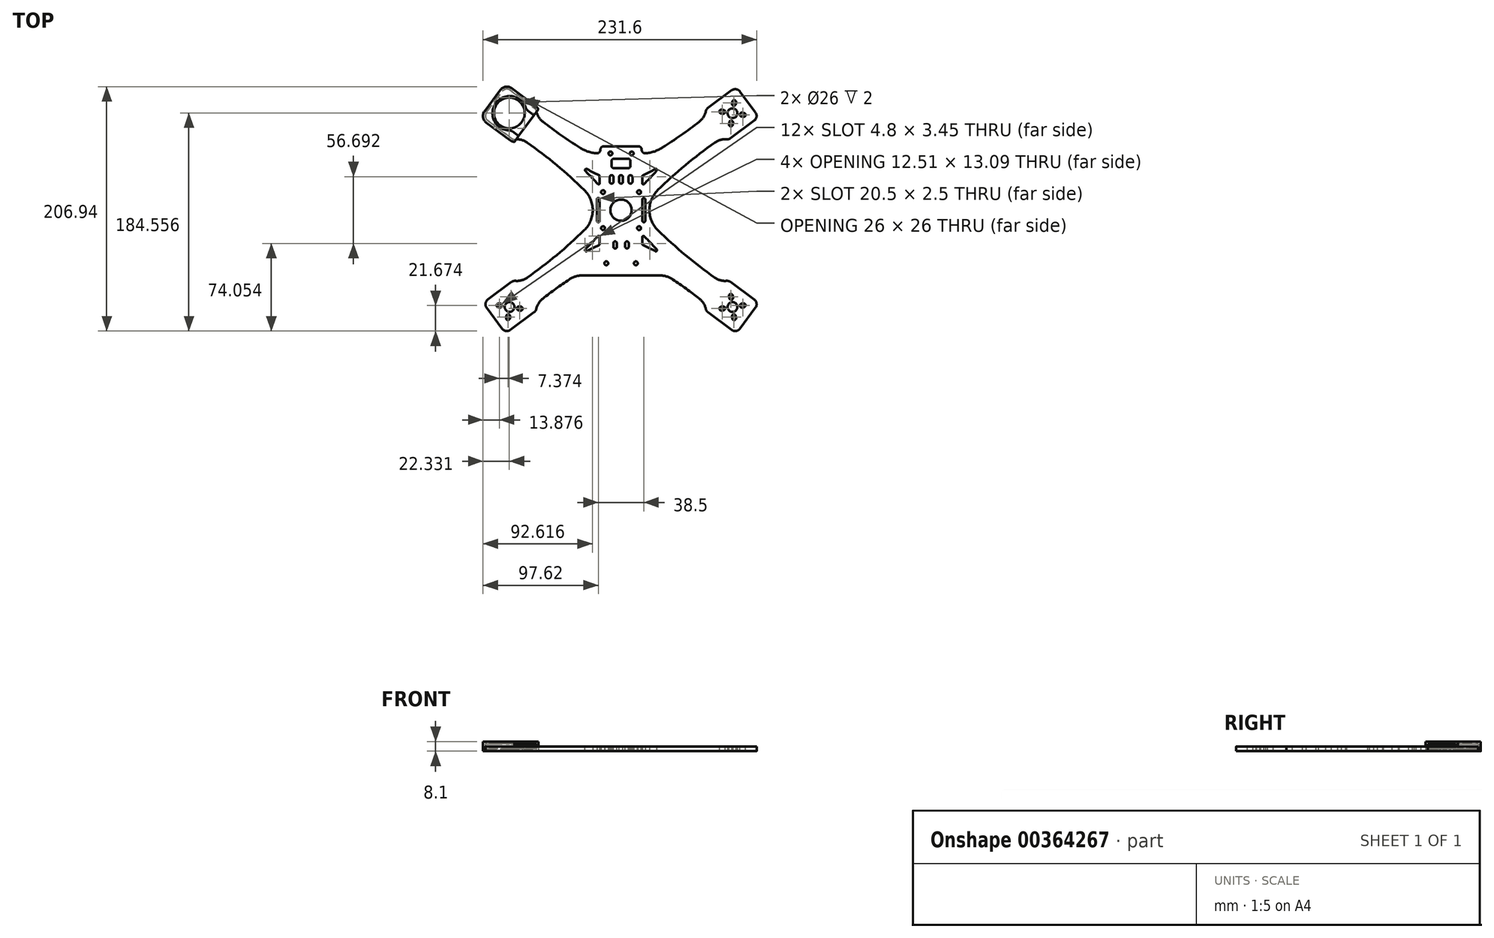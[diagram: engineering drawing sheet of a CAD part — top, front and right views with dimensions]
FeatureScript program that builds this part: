
annotation { "Feature Type Name" : "Feature", "Feature Type Description" : "" }
export const myFeature = defineFeature(function(context is Context, id is Id, definition is map)
    precondition{}
    {
        {
            var Q0;
            Q0=qCreatedBy(makeId("Top.planeOp"),FACE);
            var sketch = newSketch(context, id + "F0", { "sketchPlane" : qUnion([Q0])});
            skCircle(sketch, "E0", {"center": v(-15.25, 15.25) * mm, "radius": 1.63 * mm});
            skCircle(sketch, "E1", {"center": v(0, 0) * mm, "radius": 125 * mm, "construction": true});
            skCircle(sketch, "E2", {"center": v(-94.34, 82) * mm, "radius": 77.5 * mm, "construction": true});
            skLineSegment(sketch, "E3", {"start": v(0, 0) * mm, "end": v(-94.34, 82) * mm, "construction": true});
            skLineSegment(sketch, "E4", {"start": v(-94.34, 82) * mm, "end": v(0, 12) * mm, "construction": true});
            skLineSegment(sketch, "E5.bottom", {"start": v(-113.74, 82.7) * mm, "end": v(-100.63, 100.38) * mm});
            skLineSegment(sketch, "E5.left", {"start": v(-112.7, 75.71) * mm, "end": v(-92.67, 60.85) * mm});
            skLineSegment(sketch, "E5.right", {"start": v(-93.64, 101.41) * mm, "end": v(-73.6, 86.54) * mm});
            skLineSegment(sketch, "E6", {"start": v(-17.5, 54) * mm, "end": v(0, 54) * mm});
            skArc(sketch, "E7", {"start": v(-71.69, 83.57) * mm, "mid": v(-69.73, 78.72) * mm, "end": v(-66.21, 74.83) * mm});
            skArc(sketch, "E8", {"start": v(-79.32, 57.17) * mm, "mid": v(-84.06, 59.4) * mm, "end": v(-89.27, 59.88) * mm});
            skLineSegment(sketch, "E9", {"start": v(-19.25, 9) * mm, "end": v(-19.25, -9) * mm, "construction": true});
            skArc(sketch, "E10.0.startCap", {"start": v(-20.5, 9) * mm, "mid": v(-19.25, 10.25) * mm, "end": v(-18, 9) * mm});
            skArc(sketch, "E10.0.endCap", {"start": v(-18, -9) * mm, "mid": v(-19.25, -10.25) * mm, "end": v(-20.5, -9) * mm});
            skLineSegment(sketch, "E10.0.left", {"start": v(-18, 9) * mm, "end": v(-18, -9) * mm});
            skLineSegment(sketch, "E10.0.right", {"start": v(-20.5, 9) * mm, "end": v(-20.5, -9) * mm});
            skPoint(sketch, "E11.visualSharp", {"position": v(-116.72, 78.7) * mm});
            skArc(sketch, "E11.filletArc", {"start": v(-113.74, 82.7) * mm, "mid": v(-114.67, 79) * mm, "end": v(-112.7, 75.71) * mm});
            skPoint(sketch, "E12.visualSharp", {"position": v(-97.65, 104.4) * mm});
            skArc(sketch, "E12.filletArc", {"start": v(-93.64, 101.41) * mm, "mid": v(-97.35, 102.34) * mm, "end": v(-100.63, 100.38) * mm});
            skPoint(sketch, "E13.visualSharp", {"position": v(-91.02, 59.62) * mm});
            skArc(sketch, "E13.filletArc", {"start": v(-92.67, 60.85) * mm, "mid": v(-91.06, 60.05) * mm, "end": v(-89.27, 59.88) * mm});
            skPoint(sketch, "E14.visualSharp", {"position": v(-71.96, 85.32) * mm});
            skArc(sketch, "E14.filletArc", {"start": v(-71.69, 83.57) * mm, "mid": v(-72.37, 85.23) * mm, "end": v(-73.6, 86.54) * mm});
            skArc(sketch, "E15.MirrorCS", {"start": v(20.5, 9) * mm, "mid": v(19.25, 10.25) * mm, "end": v(18, 9) * mm});
            skArc(sketch, "E16.MirrorCS", {"start": v(71.69, 83.57) * mm, "mid": v(72.37, 85.23) * mm, "end": v(73.6, 86.54) * mm});
            skArc(sketch, "E17.MirrorCS", {"start": v(18, -9) * mm, "mid": v(19.25, -10.25) * mm, "end": v(20.5, -9) * mm});
            skArc(sketch, "E18.MirrorCS", {"start": v(92.67, 60.85) * mm, "mid": v(91.06, 60.05) * mm, "end": v(89.27, 59.88) * mm});
            skArc(sketch, "E19.MirrorCS", {"start": v(113.74, 82.7) * mm, "mid": v(114.67, 79) * mm, "end": v(112.7, 75.71) * mm});
            skArc(sketch, "E20.MirrorCS", {"start": v(71.69, 83.57) * mm, "mid": v(69.73, 78.72) * mm, "end": v(66.21, 74.83) * mm});
            skArc(sketch, "E21.MirrorCS", {"start": v(93.64, 101.41) * mm, "mid": v(97.35, 102.34) * mm, "end": v(100.63, 100.38) * mm});
            skArc(sketch, "E22.MirrorCS", {"start": v(79.32, 57.17) * mm, "mid": v(84.06, 59.4) * mm, "end": v(89.27, 59.88) * mm});
            skLineSegment(sketch, "E23.MirrorCS", {"start": v(20.5, 9) * mm, "end": v(20.5, -9) * mm});
            skLineSegment(sketch, "E24.MirrorCS", {"start": v(18, 9) * mm, "end": v(18, -9) * mm});
            skLineSegment(sketch, "E25.MirrorCS", {"start": v(19.25, 9) * mm, "end": v(19.25, -9) * mm, "construction": true});
            skLineSegment(sketch, "E26.MirrorCS", {"start": v(17.5, 54) * mm, "end": v(0, 54) * mm});
            skCircle(sketch, "E27.MirrorC", {"center": v(15.25, 15.25) * mm, "radius": 1.63 * mm});
            skPoint(sketch, "E28.MirrorP", {"position": v(71.96, 85.32) * mm});
            skLineSegment(sketch, "E29.MirrorCS", {"start": v(113.74, 82.7) * mm, "end": v(100.63, 100.38) * mm});
            skLineSegment(sketch, "E30.MirrorCS", {"start": v(0, 0) * mm, "end": v(94.34, 82) * mm, "construction": true});
            skLineSegment(sketch, "E31.MirrorCS", {"start": v(94.34, 82) * mm, "end": v(0, 12) * mm, "construction": true});
            skCircle(sketch, "E32.MirrorC", {"center": v(94.34, 82) * mm, "radius": 77.5 * mm, "construction": true});
            skLineSegment(sketch, "E33.MirrorCS", {"start": v(112.7, 75.71) * mm, "end": v(92.67, 60.85) * mm});
            skLineSegment(sketch, "E34.MirrorCS", {"start": v(93.64, 101.41) * mm, "end": v(73.6, 86.54) * mm});
            skPoint(sketch, "E35.MirrorP", {"position": v(97.65, 104.4) * mm});
            skPoint(sketch, "E36.MirrorP", {"position": v(91.02, 59.62) * mm});
            skPoint(sketch, "E37.MirrorP", {"position": v(116.72, 78.7) * mm});
            skArc(sketch, "E38.MirrorCS", {"start": v(-71.69, -83.57) * mm, "mid": v(-72.37, -85.23) * mm, "end": v(-73.6, -86.54) * mm});
            skArc(sketch, "E39.MirrorCS", {"start": v(-92.67, -60.85) * mm, "mid": v(-91.06, -60.05) * mm, "end": v(-89.27, -59.88) * mm});
            skArc(sketch, "E40.MirrorCS", {"start": v(71.69, -83.57) * mm, "mid": v(72.37, -85.23) * mm, "end": v(73.6, -86.54) * mm});
            skArc(sketch, "E41.MirrorCS", {"start": v(92.67, -60.85) * mm, "mid": v(91.06, -60.05) * mm, "end": v(89.27, -59.88) * mm});
            skArc(sketch, "E42.MirrorCS", {"start": v(79.32, -57.17) * mm, "mid": v(84.06, -59.4) * mm, "end": v(89.27, -59.88) * mm});
            skArc(sketch, "E43.MirrorCS", {"start": v(93.64, -101.41) * mm, "mid": v(97.35, -102.34) * mm, "end": v(100.63, -100.38) * mm});
            skArc(sketch, "E44.MirrorCS", {"start": v(-93.64, -101.41) * mm, "mid": v(-97.35, -102.34) * mm, "end": v(-100.63, -100.38) * mm});
            skArc(sketch, "E45.MirrorCS", {"start": v(-79.32, -57.17) * mm, "mid": v(-84.06, -59.4) * mm, "end": v(-89.27, -59.88) * mm});
            skArc(sketch, "E46.MirrorCS", {"start": v(-71.69, -83.57) * mm, "mid": v(-69.73, -78.72) * mm, "end": v(-66.21, -74.83) * mm});
            skArc(sketch, "E47.MirrorCS", {"start": v(113.74, -82.7) * mm, "mid": v(114.67, -79) * mm, "end": v(112.7, -75.71) * mm});
            skArc(sketch, "E48.MirrorCS", {"start": v(71.69, -83.57) * mm, "mid": v(69.73, -78.72) * mm, "end": v(66.21, -74.83) * mm});
            skArc(sketch, "E49.MirrorCS", {"start": v(-113.74, -82.7) * mm, "mid": v(-114.67, -79) * mm, "end": v(-112.7, -75.71) * mm});
            skCircle(sketch, "E50.MirrorC", {"center": v(-15.25, -15.25) * mm, "radius": 1.63 * mm});
            skCircle(sketch, "E51.MirrorC", {"center": v(15.25, -15.25) * mm, "radius": 1.63 * mm});
            skPoint(sketch, "E52.MirrorP", {"position": v(-71.96, -85.32) * mm});
            skLineSegment(sketch, "E53.MirrorCS", {"start": v(93.64, -101.41) * mm, "end": v(73.6, -86.54) * mm});
            skPoint(sketch, "E54.MirrorP", {"position": v(116.72, -78.7) * mm});
            skLineSegment(sketch, "E55.MirrorCS", {"start": v(112.7, -75.71) * mm, "end": v(92.67, -60.85) * mm});
            skPoint(sketch, "E56.MirrorP", {"position": v(91.02, -59.62) * mm});
            skPoint(sketch, "E57.MirrorP", {"position": v(-91.02, -59.62) * mm});
            skLineSegment(sketch, "E58.MirrorCS", {"start": v(-93.64, -101.41) * mm, "end": v(-73.6, -86.54) * mm});
            skLineSegment(sketch, "E59.MirrorCS", {"start": v(-112.7, -75.71) * mm, "end": v(-92.67, -60.85) * mm});
            skLineSegment(sketch, "E60.MirrorCS", {"start": v(-113.74, -82.7) * mm, "end": v(-100.63, -100.38) * mm});
            skPoint(sketch, "E61.MirrorP", {"position": v(-97.65, -104.4) * mm});
            skLineSegment(sketch, "E62.MirrorCS", {"start": v(113.74, -82.7) * mm, "end": v(100.63, -100.38) * mm});
            skPoint(sketch, "E63.MirrorP", {"position": v(97.65, -104.4) * mm});
            skPoint(sketch, "E64.MirrorP", {"position": v(-116.72, -78.7) * mm});
            skPoint(sketch, "E65.MirrorP", {"position": v(71.96, -85.32) * mm});
            skCircle(sketch, "E66.MirrorC", {"center": v(-94.34, -82) * mm, "radius": 77.5 * mm, "construction": true});
            skCircle(sketch, "E67.MirrorC", {"center": v(94.34, -82) * mm, "radius": 77.5 * mm, "construction": true});
            skCircle(sketch, "E68", {"center": v(-94.34, 82) * mm, "radius": 4.12 * mm});
            skCircle(sketch, "E69.MirrorC", {"center": v(94.34, 82) * mm, "radius": 4.12 * mm});
            skCircle(sketch, "E70.MirrorC", {"center": v(-94.34, -82) * mm, "radius": 4.12 * mm});
            skCircle(sketch, "E71.MirrorC", {"center": v(94.34, -82) * mm, "radius": 4.12 * mm});
            skArc(sketch, "E72", {"start": v(-31.15, 16.99) * mm, "mid": v(-54.45, 38.02) * mm, "end": v(-79.32, 57.17) * mm});
            skArc(sketch, "E73.MirrorCS", {"start": v(31.15, 16.99) * mm, "mid": v(54.45, 38.02) * mm, "end": v(79.32, 57.17) * mm});
            skArc(sketch, "E74.MirrorCS", {"start": v(-31.15, -16.99) * mm, "mid": v(-54.45, -38.02) * mm, "end": v(-79.32, -57.17) * mm});
            skArc(sketch, "E75.MirrorCS", {"start": v(31.15, -16.99) * mm, "mid": v(54.45, -38.02) * mm, "end": v(79.32, -57.17) * mm});
            skArc(sketch, "E76.trimOffspring", {"start": v(-34.92, 52.85) * mm, "mid": v(-50.83, 63.47) * mm, "end": v(-66.21, 74.83) * mm});
            skArc(sketch, "E77.MirrorCS", {"start": v(34.92, 52.85) * mm, "mid": v(50.83, 63.47) * mm, "end": v(66.21, 74.83) * mm});
            skArc(sketch, "E78.MirrorCS", {"start": v(43.8, -58.64) * mm, "mid": v(55.14, -66.54) * mm, "end": v(66.21, -74.83) * mm});
            skArc(sketch, "E79.MirrorCS", {"start": v(-43.8, -58.64) * mm, "mid": v(-55.14, -66.54) * mm, "end": v(-66.21, -74.83) * mm});
            skLineSegment(sketch, "E80", {"start": v(-32.65, -55.25) * mm, "end": v(32.65, -55.25) * mm});
            skPoint(sketch, "E81.visualSharp", {"position": v(-38.65, -55.25) * mm});
            skArc(sketch, "E81.filletArc", {"start": v(-32.65, -55.25) * mm, "mid": v(-38.48, -56.12) * mm, "end": v(-43.8, -58.64) * mm});
            skPoint(sketch, "E82.visualSharp", {"position": v(38.65, -55.25) * mm});
            skArc(sketch, "E82.filletArc", {"start": v(43.8, -58.64) * mm, "mid": v(38.48, -56.12) * mm, "end": v(32.65, -55.25) * mm});
            skArc(sketch, "E83.filletArc", {"start": v(-34.92, 52.85) * mm, "mid": v(-28.12, 49.62) * mm, "end": v(-20.75, 48.1) * mm});
            skArc(sketch, "E84.filletArc", {"start": v(20.75, 48.1) * mm, "mid": v(28.12, 49.62) * mm, "end": v(34.92, 52.85) * mm});
            skCircle(sketch, "E85", {"center": v(-9, 48) * mm, "radius": 1.63 * mm});
            skLineSegment(sketch, "E86", {"start": v(-17.5, 54) * mm, "end": v(-17.5, 51.1) * mm});
            skLineSegment(sketch, "E87", {"start": v(17.5, 54) * mm, "end": v(17.5, 51.1) * mm});
            skPoint(sketch, "E88.visualSharp", {"position": v(-17.5, 48) * mm});
            skArc(sketch, "E88.filletArc", {"start": v(-20.75, 48.1) * mm, "mid": v(-18.47, 48.88) * mm, "end": v(-17.5, 51.1) * mm});
            skPoint(sketch, "E89.visualSharp", {"position": v(17.5, 48) * mm});
            skArc(sketch, "E89.filletArc", {"start": v(17.5, 51.1) * mm, "mid": v(18.47, 48.88) * mm, "end": v(20.75, 48.1) * mm});
            skCircle(sketch, "E90.MirrorC", {"center": v(9, 48) * mm, "radius": 1.63 * mm});
            skPoint(sketch, "E91.visualSharp", {"position": v(-14.76, 0) * mm});
            skArc(sketch, "E91.filletArc", {"start": v(-31.15, -16.99) * mm, "mid": v(-24, 0) * mm, "end": v(-31.15, 16.99) * mm});
            skPoint(sketch, "E92.visualSharp", {"position": v(14.76, 0) * mm});
            skArc(sketch, "E92.filletArc", {"start": v(31.15, 16.99) * mm, "mid": v(24, 0) * mm, "end": v(31.15, -16.99) * mm});
            skCircle(sketch, "E93", {"center": v(-12.5, -45) * mm, "radius": 1.63 * mm});
            skCircle(sketch, "E94.MirrorC", {"center": v(12.5, -45) * mm, "radius": 1.63 * mm});
            skSolve(sketch);
        }
        {
            var Q0;
            Q0=qSketchRegion(id+"F0",true);
            extrude(context, id + "F1", {"entities" : qUnion([Q0]), "depth" : 4 * mm});
        }
        {
            var Q0;
            Q0=makeQuery(id+"F1.opExtrude","CAP_FACE",FACE,{"disambiguationData":[OSD([sQuery(id+"F0.wireOp",EDGE,"E0"),sQuery(id+"F0.wireOp",EDGE,"bZv11kwC-7Zwh-qoiM-MuVD-QWfY3VRXTvEb"),sQuery(id+"F0.wireOp",EDGE,"Hg7IfRWj-3ALA-Ly6Y-QmXC-kUpIx1ZQ4bFj"),sQuery(id+"F0.wireOp",EDGE,"i2Ly1i0H-hUQD-DSDW-V0AA-PaiG6Uw8rzNW"),sQuery(id+"F0.wireOp",EDGE,"E5.bottom"),sQuery(id+"F0.wireOp",EDGE,"E5.left"),sQuery(id+"F0.wireOp",EDGE,"E5.right"),sQuery(id+"F0.wireOp",EDGE,"E7"),sQuery(id+"F0.wireOp",EDGE,"E8"),sQuery(id+"F0.wireOp",EDGE,"26a3e7e2-4a16-4030-acf8-3f1fbd5a5a34.filletArc"),sQuery(id+"F0.wireOp",EDGE,"E10.0.startCap"),sQuery(id+"F0.wireOp",EDGE,"E10.0.endCap"),sQuery(id+"F0.wireOp",EDGE,"E10.0.left"),sQuery(id+"F0.wireOp",EDGE,"E10.0.right"),sQuery(id+"F0.wireOp",EDGE,"E11.filletArc"),sQuery(id+"F0.wireOp",EDGE,"E12.filletArc"),sQuery(id+"F0.wireOp",EDGE,"E13.filletArc"),sQuery(id+"F0.wireOp",EDGE,"E14.filletArc"),sQuery(id+"F0.wireOp",EDGE,"E15.MirrorCS"),sQuery(id+"F0.wireOp",EDGE,"E16.MirrorCS"),sQuery(id+"F0.wireOp",EDGE,"E17.MirrorCS"),sQuery(id+"F0.wireOp",EDGE,"E18.MirrorCS"),sQuery(id+"F0.wireOp",EDGE,"E19.MirrorCS"),sQuery(id+"F0.wireOp",EDGE,"E20.MirrorCS"),sQuery(id+"F0.wireOp",EDGE,"b7ecff87-ac14-4935-8a3e-caa413c79c2e13.MirrorCS"),sQuery(id+"F0.wireOp",EDGE,"E21.MirrorCS"),sQuery(id+"F0.wireOp",EDGE,"E22.MirrorCS"),sQuery(id+"F0.wireOp",EDGE,"E23.MirrorCS"),sQuery(id+"F0.wireOp",EDGE,"E24.MirrorCS"),sQuery(id+"F0.wireOp",EDGE,"b7ecff87-ac14-4935-8a3e-caa413c79c2e23.MirrorCS"),sQuery(id+"F0.wireOp",EDGE,"E27.MirrorC"),sQuery(id+"F0.wireOp",EDGE,"E29.MirrorCS"),sQuery(id+"F0.wireOp",EDGE,"b7ecff87-ac14-4935-8a3e-caa413c79c2e29.MirrorCS"),sQuery(id+"F0.wireOp",EDGE,"E33.MirrorCS"),sQuery(id+"F0.wireOp",EDGE,"E34.MirrorCS"),sQuery(id+"F0.wireOp",EDGE,"b7ecff87-ac14-4935-8a3e-caa413c79c2e39.MirrorCS"),sQuery(id+"F0.wireOp",EDGE,"E38.MirrorCS"),sQuery(id+"F0.wireOp",EDGE,"E39.MirrorCS"),sQuery(id+"F0.wireOp",EDGE,"E40.MirrorCS"),sQuery(id+"F0.wireOp",EDGE,"E41.MirrorCS"),sQuery(id+"F0.wireOp",EDGE,"E42.MirrorCS"),sQuery(id+"F0.wireOp",EDGE,"E43.MirrorCS"),sQuery(id+"F0.wireOp",EDGE,"E44.MirrorCS"),sQuery(id+"F0.wireOp",EDGE,"E45.MirrorCS"),sQuery(id+"F0.wireOp",EDGE,"E46.MirrorCS"),sQuery(id+"F0.wireOp",EDGE,"E47.MirrorCS"),sQuery(id+"F0.wireOp",EDGE,"E48.MirrorCS"),sQuery(id+"F0.wireOp",EDGE,"E49.MirrorCS"),sQuery(id+"F0.wireOp",EDGE,"E50.MirrorC"),sQuery(id+"F0.wireOp",EDGE,"E51.MirrorC"),sQuery(id+"F0.wireOp",EDGE,"7b8357ce-6b81-4621-bb5f-09712327f37e37.MirrorCS"),sQuery(id+"F0.wireOp",EDGE,"E53.MirrorCS"),sQuery(id+"F0.wireOp",EDGE,"E55.MirrorCS"),sQuery(id+"F0.wireOp",EDGE,"E58.MirrorCS"),sQuery(id+"F0.wireOp",EDGE,"E59.MirrorCS"),sQuery(id+"F0.wireOp",EDGE,"E60.MirrorCS"),sQuery(id+"F0.wireOp",EDGE,"7b8357ce-6b81-4621-bb5f-09712327f37e49.MirrorCS"),sQuery(id+"F0.wireOp",EDGE,"7b8357ce-6b81-4621-bb5f-09712327f37e50.MirrorCS"),sQuery(id+"F0.wireOp",EDGE,"E62.MirrorCS"),sQuery(id+"F0.wireOp",EDGE,"7b8357ce-6b81-4621-bb5f-09712327f37e55.MirrorCS"),sQuery(id+"F0.wireOp",EDGE,"d83ce2ea-2607-4b6c-a04d-38c7ae4304c90.MirrorCS"),sQuery(id+"F0.wireOp",EDGE,"b69c18a7-e43b-42be-b145-92b5204aa2ed0.MirrorCS"),sQuery(id+"F0.wireOp",EDGE,"a0707623-7043-4475-b436-6124989390590.MirrorCS"),sQuery(id+"F0.wireOp",EDGE,"4f61c261-c1ce-4229-8802-2f54477ed9b20.MirrorCS"),sQuery(id+"F0.wireOp",EDGE,"PiAP6XZh-xq8d-wj9O-Epc7-kF4WUdjTUHBz"),sQuery(id+"F0.wireOp",EDGE,"26e37ba6-caeb-4f33-ab48-1d1fe7035cbd0.MirrorC"),sQuery(id+"F0.wireOp",EDGE,"2yan8IeJ-tOHB-Kgj5-MnLH-DyiSyil4pG3S"),sQuery(id+"F0.wireOp",EDGE,"gHJ05LQx-usyR-kV3a-hPzh-QXjW5T1wXW1p"),sQuery(id+"F0.wireOp",EDGE,"uchXSoDE-KjdM-uTwm-rJXX-9rzWfyOP3x4Z"),sQuery(id+"F0.wireOp",EDGE,"8eu2Gxre-rbZ0-mDo1-W97T-pc3IviFYihye"),sQuery(id+"F0.wireOp",EDGE,"eavqlNsN-eOFr-pDPr-DEgw-YRCTYlhg5u3t"),sQuery(id+"F0.wireOp",EDGE,"Bw8slYh4-NEub-OYFD-4ET6-0dd0G63bUOwi"),sQuery(id+"F0.wireOp",EDGE,"af94888a-cba0-45cd-aecc-a0270221dd82.trimOffspring"),sQuery(id+"F0.wireOp",EDGE,"36199e4a-d6a7-49c4-a502-27b3488fd5e6.filletArc"),sQuery(id+"F0.wireOp",EDGE,"9e30e6b1-65ef-4937-9bd8-18fed2c5f1090.MirrorCS"),sQuery(id+"F0.wireOp",EDGE,"31f30485-6f3e-4795-917b-55e225d339680.MirrorCS"),sQuery(id+"F0.wireOp",EDGE,"86aa6092-d3c3-42aa-99ce-90435510c5960.MirrorCS"),sQuery(id+"F0.wireOp",EDGE,"5a69975c-1d9b-4b23-809c-878e26df679d0.MirrorCS"),sQuery(id+"F0.wireOp",EDGE,"8025df49-7d22-4dba-957a-6396c4b11ce90.MirrorCS"),sQuery(id+"F0.wireOp",EDGE,"b23088bf-ab4c-4e44-9a43-da8ffa8499a00.MirrorCS"),sQuery(id+"F0.wireOp",EDGE,"d9780cfa-9ead-4347-a629-1b1a594d6e410.MirrorCS"),sQuery(id+"F0.wireOp",EDGE,"68fec51b-96b4-4918-b858-b07c475e679e0.MirrorCS"),sQuery(id+"F0.wireOp",EDGE,"b72a6ee6-5ab0-4ed6-be8f-ffada714514d0.MirrorCS"),sQuery(id+"F0.wireOp",EDGE,"8773bbf2-5ef2-485a-bde0-34addb67332b0.MirrorCS"),sQuery(id+"F0.wireOp",EDGE,"ce348970-fad1-4eb4-9c27-5204bf570fdb0.MirrorCS"),sQuery(id+"F0.wireOp",EDGE,"404c4f6d-7f85-4f91-8924-7a461248f6590.MirrorCS"),sQuery(id+"F0.wireOp",EDGE,"TJ6xSgkY-RBVc-ApbF-Rnxn-nYxT4uNRJTxX"),sQuery(id+"F0.wireOp",EDGE,"hn5H7zRm-rU73-VfAX-dvYv-k9Lax7dM8k8G"),sQuery(id+"F0.wireOp",EDGE,"UOzbpYJr-Rpqu-ZeE8-tXKC-t89DSqlBGB8Q"),sQuery(id+"F0.wireOp",EDGE,"YxJJHRqV-amlc-LN3y-haml-tisoirnnfRJY"),sQuery(id+"F0.wireOp",EDGE,"033e0fe7-d3c1-42f5-ae8f-adbb043379e8.filletArc"),sQuery(id+"F0.wireOp",EDGE,"afa99035-e99d-4a73-974f-5500cdf2138a.filletArc"),sQuery(id+"F0.wireOp",EDGE,"9i3ea3iE-3Dll-Ek6R-PhGe-V1XcnAEkodY1.bottom"),sQuery(id+"F0.wireOp",EDGE,"9i3ea3iE-3Dll-Ek6R-PhGe-V1XcnAEkodY1.left"),sQuery(id+"F0.wireOp",EDGE,"9i3ea3iE-3Dll-Ek6R-PhGe-V1XcnAEkodY1.right"),sQuery(id+"F0.wireOp",EDGE,"1382622d-cae2-4c61-9f5c-b8746732d9fe0.MirrorCS"),sQuery(id+"F0.wireOp",EDGE,"0d70f9a0-c1ad-434e-a495-165a5a764f960.MirrorCS"),sQuery(id+"F0.wireOp",EDGE,"1f8d5036-162d-4fc3-b441-7a8ab5cd179e0.MirrorCS"),sQuery(id+"F0.wireOp",EDGE,"Km0E7gO1-P8tX-SnyZ-vo1L-W35BEzFtr7vK"),sQuery(id+"F0.wireOp",EDGE,"4twT0r3F-PA9R-wz1e-iyg0-9RBk79VGwi7g"),sQuery(id+"F0.wireOp",EDGE,"14bccf5c-bb99-48c5-a73f-577480a40b4e0.MirrorCS"),sQuery(id+"F0.wireOp",EDGE,"a123c59d-a695-4b06-9137-5aaff9e2b4be0.MirrorCS"),sQuery(id+"F0.wireOp",EDGE,"E68"),sQuery(id+"F0.wireOp",EDGE,"E69.MirrorC"),sQuery(id+"F0.wireOp",EDGE,"E70.MirrorC"),sQuery(id+"F0.wireOp",EDGE,"E71.MirrorC")])],"isStart":false});
            var sketch = newSketch(context, id + "F2", { "sketchPlane" : qUnion([Q0])});
            skCircle(sketch, "E95", {"center": v(-94.34, 82) * mm, "radius": 7.95 * mm, "construction": true});
            skCircle(sketch, "E96", {"center": v(-94.34, 82) * mm, "radius": 9.55 * mm, "construction": true});
            skLineSegment(sketch, "E97", {"start": v(-95.5, 89.87) * mm, "end": v(-95.74, 91.45) * mm, "construction": true});
            skLineSegment(sketch, "E98", {"start": v(-95.5, 89.87) * mm, "end": v(-94.34, 82) * mm, "construction": true});
            skLineSegment(sketch, "E99", {"start": v(-94.34, 82) * mm, "end": v(0, 12) * mm, "construction": true});
            skArc(sketch, "E100.0.startCap", {"start": v(-93.9, 90.1) * mm, "mid": v(-95.27, 88.26) * mm, "end": v(-97.11, 89.63) * mm});
            skArc(sketch, "E100.0.endCap", {"start": v(-97.34, 91.22) * mm, "mid": v(-95.98, 93.06) * mm, "end": v(-94.13, 91.7) * mm});
            skLineSegment(sketch, "E100.0.left", {"start": v(-97.11, 89.63) * mm, "end": v(-97.34, 91.22) * mm});
            skLineSegment(sketch, "E100.0.right", {"start": v(-93.9, 90.1) * mm, "end": v(-94.13, 91.7) * mm});
            skLineSegment(sketch, "E101.1.0", {"start": v(-102.2, 80.84) * mm, "end": v(-103.79, 80.6) * mm, "construction": true});
            skArc(sketch, "E101.1.1", {"start": v(-102.44, 82.45) * mm, "mid": v(-100.6, 81.08) * mm, "end": v(-101.96, 79.24) * mm});
            skLineSegment(sketch, "E101.1.2", {"start": v(-101.96, 79.24) * mm, "end": v(-103.55, 79) * mm});
            skLineSegment(sketch, "E101.1.3", {"start": v(-102.44, 82.45) * mm, "end": v(-104.02, 82.22) * mm});
            skArc(sketch, "E101.1.4", {"start": v(-103.55, 79) * mm, "mid": v(-105.4, 80.37) * mm, "end": v(-104.02, 82.22) * mm});
            skLineSegment(sketch, "E101.2.0", {"start": v(-93.17, 74.14) * mm, "end": v(-92.94, 72.56) * mm, "construction": true});
            skArc(sketch, "E101.2.1", {"start": v(-94.78, 73.9) * mm, "mid": v(-93.41, 75.75) * mm, "end": v(-91.57, 74.38) * mm});
            skLineSegment(sketch, "E101.2.2", {"start": v(-91.57, 74.38) * mm, "end": v(-91.33, 72.8) * mm});
            skLineSegment(sketch, "E101.2.3", {"start": v(-94.78, 73.9) * mm, "end": v(-94.55, 72.32) * mm});
            skArc(sketch, "E101.2.4", {"start": v(-91.33, 72.8) * mm, "mid": v(-92.7, 70.95) * mm, "end": v(-94.55, 72.32) * mm});
            skLineSegment(sketch, "E101.3.0", {"start": v(-86.47, 83.17) * mm, "end": v(-84.9, 83.4) * mm, "construction": true});
            skArc(sketch, "E101.3.1", {"start": v(-86.24, 81.56) * mm, "mid": v(-88.08, 82.93) * mm, "end": v(-86.71, 84.78) * mm});
            skLineSegment(sketch, "E101.3.2", {"start": v(-86.71, 84.78) * mm, "end": v(-85.13, 85.01) * mm});
            skLineSegment(sketch, "E101.3.3", {"start": v(-86.24, 81.56) * mm, "end": v(-84.65, 81.8) * mm});
            skArc(sketch, "E101.3.4", {"start": v(-85.13, 85.01) * mm, "mid": v(-83.28, 83.64) * mm, "end": v(-84.65, 81.8) * mm});
            skLineSegment(sketch, "E102.MirrorCS", {"start": v(95.5, 89.87) * mm, "end": v(95.74, 91.45) * mm, "construction": true});
            skLineSegment(sketch, "E103.MirrorCS", {"start": v(93.9, 90.1) * mm, "end": v(94.13, 91.7) * mm});
            skLineSegment(sketch, "E104.MirrorCS", {"start": v(102.2, 80.84) * mm, "end": v(103.79, 80.6) * mm, "construction": true});
            skLineSegment(sketch, "E105.MirrorCS", {"start": v(102.44, 82.45) * mm, "end": v(104.02, 82.22) * mm});
            skLineSegment(sketch, "E106.MirrorCS", {"start": v(86.71, 84.78) * mm, "end": v(85.13, 85.01) * mm});
            skLineSegment(sketch, "E107.MirrorCS", {"start": v(97.11, 89.63) * mm, "end": v(97.34, 91.22) * mm});
            skLineSegment(sketch, "E108.MirrorCS", {"start": v(94.78, 73.9) * mm, "end": v(94.55, 72.32) * mm});
            skLineSegment(sketch, "E109.MirrorCS", {"start": v(86.24, 81.56) * mm, "end": v(84.65, 81.8) * mm});
            skArc(sketch, "E110.MirrorCS", {"start": v(102.44, 82.45) * mm, "mid": v(100.6, 81.08) * mm, "end": v(101.96, 79.24) * mm});
            skArc(sketch, "E111.MirrorCS", {"start": v(97.34, 91.22) * mm, "mid": v(95.98, 93.06) * mm, "end": v(94.13, 91.7) * mm});
            skArc(sketch, "E112.MirrorCS", {"start": v(91.33, 72.8) * mm, "mid": v(92.7, 70.95) * mm, "end": v(94.55, 72.32) * mm});
            skLineSegment(sketch, "E113.MirrorCS", {"start": v(93.17, 74.14) * mm, "end": v(92.94, 72.56) * mm, "construction": true});
            skArc(sketch, "E114.MirrorCS", {"start": v(85.13, 85.01) * mm, "mid": v(83.28, 83.64) * mm, "end": v(84.65, 81.8) * mm});
            skArc(sketch, "E115.MirrorCS", {"start": v(103.55, 79) * mm, "mid": v(105.4, 80.37) * mm, "end": v(104.02, 82.22) * mm});
            skLineSegment(sketch, "E116.MirrorCS", {"start": v(86.47, 83.17) * mm, "end": v(84.9, 83.4) * mm, "construction": true});
            skLineSegment(sketch, "E117.MirrorCS", {"start": v(101.96, 79.24) * mm, "end": v(103.55, 79) * mm});
            skArc(sketch, "E118.MirrorCS", {"start": v(94.78, 73.9) * mm, "mid": v(93.41, 75.75) * mm, "end": v(91.57, 74.38) * mm});
            skArc(sketch, "E119.MirrorCS", {"start": v(86.24, 81.56) * mm, "mid": v(88.08, 82.93) * mm, "end": v(86.71, 84.78) * mm});
            skLineSegment(sketch, "E120.MirrorCS", {"start": v(91.57, 74.38) * mm, "end": v(91.33, 72.8) * mm});
            skArc(sketch, "E121.MirrorCS", {"start": v(93.9, 90.1) * mm, "mid": v(95.27, 88.26) * mm, "end": v(97.11, 89.63) * mm});
            skPoint(sketch, "E122.MirrorP", {"position": v(94.34, 82) * mm});
            skCircle(sketch, "E123.MirrorC", {"center": v(94.34, 82) * mm, "radius": 9.55 * mm, "construction": true});
            skCircle(sketch, "E124.MirrorC", {"center": v(94.34, 82) * mm, "radius": 7.95 * mm, "construction": true});
            skLineSegment(sketch, "E125.MirrorCS", {"start": v(95.5, 89.87) * mm, "end": v(94.34, 82) * mm, "construction": true});
            skLineSegment(sketch, "E126.MirrorCS", {"start": v(-95.5, -89.87) * mm, "end": v(-95.74, -91.45) * mm, "construction": true});
            skLineSegment(sketch, "E127.MirrorCS", {"start": v(-93.9, -90.1) * mm, "end": v(-94.13, -91.7) * mm});
            skArc(sketch, "E128.MirrorCS", {"start": v(-93.9, -90.1) * mm, "mid": v(-95.27, -88.26) * mm, "end": v(-97.11, -89.63) * mm});
            skLineSegment(sketch, "E129.MirrorCS", {"start": v(-95.5, -89.87) * mm, "end": v(-94.34, -82) * mm, "construction": true});
            skLineSegment(sketch, "E130.MirrorCS", {"start": v(-97.11, -89.63) * mm, "end": v(-97.34, -91.22) * mm});
            skLineSegment(sketch, "E131.MirrorCS", {"start": v(-102.44, -82.45) * mm, "end": v(-104.02, -82.22) * mm});
            skLineSegment(sketch, "E132.MirrorCS", {"start": v(86.24, -81.56) * mm, "end": v(84.65, -81.8) * mm});
            skArc(sketch, "E133.MirrorCS", {"start": v(86.24, -81.56) * mm, "mid": v(88.08, -82.93) * mm, "end": v(86.71, -84.78) * mm});
            skLineSegment(sketch, "E134.MirrorCS", {"start": v(97.11, -89.63) * mm, "end": v(97.34, -91.22) * mm});
            skArc(sketch, "E135.MirrorCS", {"start": v(-102.44, -82.45) * mm, "mid": v(-100.6, -81.08) * mm, "end": v(-101.96, -79.24) * mm});
            skLineSegment(sketch, "E136.MirrorCS", {"start": v(-101.96, -79.24) * mm, "end": v(-103.55, -79) * mm});
            skLineSegment(sketch, "E137.MirrorCS", {"start": v(-102.2, -80.84) * mm, "end": v(-103.79, -80.6) * mm, "construction": true});
            skArc(sketch, "E138.MirrorCS", {"start": v(-103.55, -79) * mm, "mid": v(-105.4, -80.37) * mm, "end": v(-104.02, -82.22) * mm});
            skLineSegment(sketch, "E139.MirrorCS", {"start": v(102.2, -80.84) * mm, "end": v(103.79, -80.6) * mm, "construction": true});
            skLineSegment(sketch, "E140.MirrorCS", {"start": v(86.47, -83.17) * mm, "end": v(84.9, -83.4) * mm, "construction": true});
            skLineSegment(sketch, "E141.MirrorCS", {"start": v(101.96, -79.24) * mm, "end": v(103.55, -79) * mm});
            skArc(sketch, "E142.MirrorCS", {"start": v(102.44, -82.45) * mm, "mid": v(100.6, -81.08) * mm, "end": v(101.96, -79.24) * mm});
            skLineSegment(sketch, "E143.MirrorCS", {"start": v(86.71, -84.78) * mm, "end": v(85.13, -85.01) * mm});
            skArc(sketch, "E144.MirrorCS", {"start": v(93.9, -90.1) * mm, "mid": v(95.27, -88.26) * mm, "end": v(97.11, -89.63) * mm});
            skLineSegment(sketch, "E145.MirrorCS", {"start": v(93.9, -90.1) * mm, "end": v(94.13, -91.7) * mm});
            skLineSegment(sketch, "E146.MirrorCS", {"start": v(102.44, -82.45) * mm, "end": v(104.02, -82.22) * mm});
            skArc(sketch, "E147.MirrorCS", {"start": v(103.55, -79) * mm, "mid": v(105.4, -80.37) * mm, "end": v(104.02, -82.22) * mm});
            skLineSegment(sketch, "E148.MirrorCS", {"start": v(95.5, -89.87) * mm, "end": v(94.34, -82) * mm, "construction": true});
            skLineSegment(sketch, "E149.MirrorCS", {"start": v(95.5, -89.87) * mm, "end": v(95.74, -91.45) * mm, "construction": true});
            skLineSegment(sketch, "E150.MirrorCS", {"start": v(91.57, -74.38) * mm, "end": v(91.33, -72.8) * mm});
            skLineSegment(sketch, "E151.MirrorCS", {"start": v(-91.57, -74.38) * mm, "end": v(-91.33, -72.8) * mm});
            skLineSegment(sketch, "E152.MirrorCS", {"start": v(-94.78, -73.9) * mm, "end": v(-94.55, -72.32) * mm});
            skArc(sketch, "E153.MirrorCS", {"start": v(-85.13, -85.01) * mm, "mid": v(-83.28, -83.64) * mm, "end": v(-84.65, -81.8) * mm});
            skArc(sketch, "E154.MirrorCS", {"start": v(97.34, -91.22) * mm, "mid": v(95.98, -93.06) * mm, "end": v(94.13, -91.7) * mm});
            skArc(sketch, "E155.MirrorCS", {"start": v(94.78, -73.9) * mm, "mid": v(93.41, -75.75) * mm, "end": v(91.57, -74.38) * mm});
            skArc(sketch, "E156.MirrorCS", {"start": v(-91.33, -72.8) * mm, "mid": v(-92.7, -70.95) * mm, "end": v(-94.55, -72.32) * mm});
            skLineSegment(sketch, "E157.MirrorCS", {"start": v(-86.71, -84.78) * mm, "end": v(-85.13, -85.01) * mm});
            skArc(sketch, "E158.MirrorCS", {"start": v(-86.24, -81.56) * mm, "mid": v(-88.08, -82.93) * mm, "end": v(-86.71, -84.78) * mm});
            skArc(sketch, "E159.MirrorCS", {"start": v(-97.34, -91.22) * mm, "mid": v(-95.98, -93.06) * mm, "end": v(-94.13, -91.7) * mm});
            skArc(sketch, "E160.MirrorCS", {"start": v(91.33, -72.8) * mm, "mid": v(92.7, -70.95) * mm, "end": v(94.55, -72.32) * mm});
            skLineSegment(sketch, "E161.MirrorCS", {"start": v(-86.47, -83.17) * mm, "end": v(-84.9, -83.4) * mm, "construction": true});
            skArc(sketch, "E162.MirrorCS", {"start": v(85.13, -85.01) * mm, "mid": v(83.28, -83.64) * mm, "end": v(84.65, -81.8) * mm});
            skArc(sketch, "E163.MirrorCS", {"start": v(-94.78, -73.9) * mm, "mid": v(-93.41, -75.75) * mm, "end": v(-91.57, -74.38) * mm});
            skLineSegment(sketch, "E164.MirrorCS", {"start": v(-86.24, -81.56) * mm, "end": v(-84.65, -81.8) * mm});
            skLineSegment(sketch, "E165.MirrorCS", {"start": v(94.78, -73.9) * mm, "end": v(94.55, -72.32) * mm});
            skLineSegment(sketch, "E166.MirrorCS", {"start": v(93.17, -74.14) * mm, "end": v(92.94, -72.56) * mm, "construction": true});
            skLineSegment(sketch, "E167.MirrorCS", {"start": v(-93.17, -74.14) * mm, "end": v(-92.94, -72.56) * mm, "construction": true});
            skCircle(sketch, "E168.MirrorC", {"center": v(94.34, -82) * mm, "radius": 7.95 * mm, "construction": true});
            skCircle(sketch, "E169.MirrorC", {"center": v(-94.34, -82) * mm, "radius": 7.95 * mm, "construction": true});
            skCircle(sketch, "E170.MirrorC", {"center": v(-94.34, -82) * mm, "radius": 9.55 * mm, "construction": true});
            skCircle(sketch, "E171.MirrorC", {"center": v(94.34, -82) * mm, "radius": 9.55 * mm, "construction": true});
            skSolve(sketch);
        }
        {
            var Q0;
            Q0 = qSketchRegion(id + "F2", true);
            extrude(context, id + "F3", {"entities" : qUnion([Q0]), "operationType" : NewBodyOperationType.REMOVE, "oppositeDirection" : true, "depth" : 25 * mm, "offsetDistance" : 25 * mm});
        }
        {
            var Q0;
            Q0=makeQuery(id+"F1.opExtrude","CAP_FACE",FACE,{"disambiguationData":[OSD([sQuery(id+"F0.wireOp",EDGE,"E0"),sQuery(id+"F0.wireOp",EDGE,"bZv11kwC-7Zwh-qoiM-MuVD-QWfY3VRXTvEb"),sQuery(id+"F0.wireOp",EDGE,"Hg7IfRWj-3ALA-Ly6Y-QmXC-kUpIx1ZQ4bFj"),sQuery(id+"F0.wireOp",EDGE,"i2Ly1i0H-hUQD-DSDW-V0AA-PaiG6Uw8rzNW"),sQuery(id+"F0.wireOp",EDGE,"E5.bottom"),sQuery(id+"F0.wireOp",EDGE,"E5.left"),sQuery(id+"F0.wireOp",EDGE,"E5.right"),sQuery(id+"F0.wireOp",EDGE,"E7"),sQuery(id+"F0.wireOp",EDGE,"E8"),sQuery(id+"F0.wireOp",EDGE,"26a3e7e2-4a16-4030-acf8-3f1fbd5a5a34.filletArc"),sQuery(id+"F0.wireOp",EDGE,"E10.0.startCap"),sQuery(id+"F0.wireOp",EDGE,"E10.0.endCap"),sQuery(id+"F0.wireOp",EDGE,"E10.0.left"),sQuery(id+"F0.wireOp",EDGE,"E10.0.right"),sQuery(id+"F0.wireOp",EDGE,"E11.filletArc"),sQuery(id+"F0.wireOp",EDGE,"E12.filletArc"),sQuery(id+"F0.wireOp",EDGE,"E13.filletArc"),sQuery(id+"F0.wireOp",EDGE,"E14.filletArc"),sQuery(id+"F0.wireOp",EDGE,"E15.MirrorCS"),sQuery(id+"F0.wireOp",EDGE,"E16.MirrorCS"),sQuery(id+"F0.wireOp",EDGE,"E17.MirrorCS"),sQuery(id+"F0.wireOp",EDGE,"E18.MirrorCS"),sQuery(id+"F0.wireOp",EDGE,"E19.MirrorCS"),sQuery(id+"F0.wireOp",EDGE,"E20.MirrorCS"),sQuery(id+"F0.wireOp",EDGE,"b7ecff87-ac14-4935-8a3e-caa413c79c2e13.MirrorCS"),sQuery(id+"F0.wireOp",EDGE,"E21.MirrorCS"),sQuery(id+"F0.wireOp",EDGE,"E22.MirrorCS"),sQuery(id+"F0.wireOp",EDGE,"E23.MirrorCS"),sQuery(id+"F0.wireOp",EDGE,"E24.MirrorCS"),sQuery(id+"F0.wireOp",EDGE,"b7ecff87-ac14-4935-8a3e-caa413c79c2e23.MirrorCS"),sQuery(id+"F0.wireOp",EDGE,"E27.MirrorC"),sQuery(id+"F0.wireOp",EDGE,"E29.MirrorCS"),sQuery(id+"F0.wireOp",EDGE,"b7ecff87-ac14-4935-8a3e-caa413c79c2e29.MirrorCS"),sQuery(id+"F0.wireOp",EDGE,"E33.MirrorCS"),sQuery(id+"F0.wireOp",EDGE,"E34.MirrorCS"),sQuery(id+"F0.wireOp",EDGE,"b7ecff87-ac14-4935-8a3e-caa413c79c2e39.MirrorCS"),sQuery(id+"F0.wireOp",EDGE,"E38.MirrorCS"),sQuery(id+"F0.wireOp",EDGE,"E39.MirrorCS"),sQuery(id+"F0.wireOp",EDGE,"E40.MirrorCS"),sQuery(id+"F0.wireOp",EDGE,"E41.MirrorCS"),sQuery(id+"F0.wireOp",EDGE,"E42.MirrorCS"),sQuery(id+"F0.wireOp",EDGE,"E43.MirrorCS"),sQuery(id+"F0.wireOp",EDGE,"E44.MirrorCS"),sQuery(id+"F0.wireOp",EDGE,"E45.MirrorCS"),sQuery(id+"F0.wireOp",EDGE,"E46.MirrorCS"),sQuery(id+"F0.wireOp",EDGE,"E47.MirrorCS"),sQuery(id+"F0.wireOp",EDGE,"E48.MirrorCS"),sQuery(id+"F0.wireOp",EDGE,"E49.MirrorCS"),sQuery(id+"F0.wireOp",EDGE,"E50.MirrorC"),sQuery(id+"F0.wireOp",EDGE,"E51.MirrorC"),sQuery(id+"F0.wireOp",EDGE,"7b8357ce-6b81-4621-bb5f-09712327f37e37.MirrorCS"),sQuery(id+"F0.wireOp",EDGE,"E53.MirrorCS"),sQuery(id+"F0.wireOp",EDGE,"E55.MirrorCS"),sQuery(id+"F0.wireOp",EDGE,"E58.MirrorCS"),sQuery(id+"F0.wireOp",EDGE,"E59.MirrorCS"),sQuery(id+"F0.wireOp",EDGE,"E60.MirrorCS"),sQuery(id+"F0.wireOp",EDGE,"7b8357ce-6b81-4621-bb5f-09712327f37e49.MirrorCS"),sQuery(id+"F0.wireOp",EDGE,"7b8357ce-6b81-4621-bb5f-09712327f37e50.MirrorCS"),sQuery(id+"F0.wireOp",EDGE,"E62.MirrorCS"),sQuery(id+"F0.wireOp",EDGE,"7b8357ce-6b81-4621-bb5f-09712327f37e55.MirrorCS"),sQuery(id+"F0.wireOp",EDGE,"d83ce2ea-2607-4b6c-a04d-38c7ae4304c90.MirrorCS"),sQuery(id+"F0.wireOp",EDGE,"b69c18a7-e43b-42be-b145-92b5204aa2ed0.MirrorCS"),sQuery(id+"F0.wireOp",EDGE,"a0707623-7043-4475-b436-6124989390590.MirrorCS"),sQuery(id+"F0.wireOp",EDGE,"4f61c261-c1ce-4229-8802-2f54477ed9b20.MirrorCS"),sQuery(id+"F0.wireOp",EDGE,"PiAP6XZh-xq8d-wj9O-Epc7-kF4WUdjTUHBz"),sQuery(id+"F0.wireOp",EDGE,"26e37ba6-caeb-4f33-ab48-1d1fe7035cbd0.MirrorC"),sQuery(id+"F0.wireOp",EDGE,"2yan8IeJ-tOHB-Kgj5-MnLH-DyiSyil4pG3S"),sQuery(id+"F0.wireOp",EDGE,"gHJ05LQx-usyR-kV3a-hPzh-QXjW5T1wXW1p"),sQuery(id+"F0.wireOp",EDGE,"uchXSoDE-KjdM-uTwm-rJXX-9rzWfyOP3x4Z"),sQuery(id+"F0.wireOp",EDGE,"8eu2Gxre-rbZ0-mDo1-W97T-pc3IviFYihye"),sQuery(id+"F0.wireOp",EDGE,"eavqlNsN-eOFr-pDPr-DEgw-YRCTYlhg5u3t"),sQuery(id+"F0.wireOp",EDGE,"Bw8slYh4-NEub-OYFD-4ET6-0dd0G63bUOwi"),sQuery(id+"F0.wireOp",EDGE,"af94888a-cba0-45cd-aecc-a0270221dd82.trimOffspring"),sQuery(id+"F0.wireOp",EDGE,"36199e4a-d6a7-49c4-a502-27b3488fd5e6.filletArc"),sQuery(id+"F0.wireOp",EDGE,"9e30e6b1-65ef-4937-9bd8-18fed2c5f1090.MirrorCS"),sQuery(id+"F0.wireOp",EDGE,"31f30485-6f3e-4795-917b-55e225d339680.MirrorCS"),sQuery(id+"F0.wireOp",EDGE,"86aa6092-d3c3-42aa-99ce-90435510c5960.MirrorCS"),sQuery(id+"F0.wireOp",EDGE,"5a69975c-1d9b-4b23-809c-878e26df679d0.MirrorCS"),sQuery(id+"F0.wireOp",EDGE,"8025df49-7d22-4dba-957a-6396c4b11ce90.MirrorCS"),sQuery(id+"F0.wireOp",EDGE,"b23088bf-ab4c-4e44-9a43-da8ffa8499a00.MirrorCS"),sQuery(id+"F0.wireOp",EDGE,"d9780cfa-9ead-4347-a629-1b1a594d6e410.MirrorCS"),sQuery(id+"F0.wireOp",EDGE,"68fec51b-96b4-4918-b858-b07c475e679e0.MirrorCS"),sQuery(id+"F0.wireOp",EDGE,"b72a6ee6-5ab0-4ed6-be8f-ffada714514d0.MirrorCS"),sQuery(id+"F0.wireOp",EDGE,"8773bbf2-5ef2-485a-bde0-34addb67332b0.MirrorCS"),sQuery(id+"F0.wireOp",EDGE,"ce348970-fad1-4eb4-9c27-5204bf570fdb0.MirrorCS"),sQuery(id+"F0.wireOp",EDGE,"404c4f6d-7f85-4f91-8924-7a461248f6590.MirrorCS"),sQuery(id+"F0.wireOp",EDGE,"TJ6xSgkY-RBVc-ApbF-Rnxn-nYxT4uNRJTxX"),sQuery(id+"F0.wireOp",EDGE,"hn5H7zRm-rU73-VfAX-dvYv-k9Lax7dM8k8G"),sQuery(id+"F0.wireOp",EDGE,"UOzbpYJr-Rpqu-ZeE8-tXKC-t89DSqlBGB8Q"),sQuery(id+"F0.wireOp",EDGE,"YxJJHRqV-amlc-LN3y-haml-tisoirnnfRJY"),sQuery(id+"F0.wireOp",EDGE,"033e0fe7-d3c1-42f5-ae8f-adbb043379e8.filletArc"),sQuery(id+"F0.wireOp",EDGE,"afa99035-e99d-4a73-974f-5500cdf2138a.filletArc"),sQuery(id+"F0.wireOp",EDGE,"9i3ea3iE-3Dll-Ek6R-PhGe-V1XcnAEkodY1.bottom"),sQuery(id+"F0.wireOp",EDGE,"9i3ea3iE-3Dll-Ek6R-PhGe-V1XcnAEkodY1.left"),sQuery(id+"F0.wireOp",EDGE,"9i3ea3iE-3Dll-Ek6R-PhGe-V1XcnAEkodY1.right"),sQuery(id+"F0.wireOp",EDGE,"1382622d-cae2-4c61-9f5c-b8746732d9fe0.MirrorCS"),sQuery(id+"F0.wireOp",EDGE,"0d70f9a0-c1ad-434e-a495-165a5a764f960.MirrorCS"),sQuery(id+"F0.wireOp",EDGE,"1f8d5036-162d-4fc3-b441-7a8ab5cd179e0.MirrorCS"),sQuery(id+"F0.wireOp",EDGE,"Km0E7gO1-P8tX-SnyZ-vo1L-W35BEzFtr7vK"),sQuery(id+"F0.wireOp",EDGE,"4twT0r3F-PA9R-wz1e-iyg0-9RBk79VGwi7g"),sQuery(id+"F0.wireOp",EDGE,"14bccf5c-bb99-48c5-a73f-577480a40b4e0.MirrorCS"),sQuery(id+"F0.wireOp",EDGE,"a123c59d-a695-4b06-9137-5aaff9e2b4be0.MirrorCS"),sQuery(id+"F0.wireOp",EDGE,"E68"),sQuery(id+"F0.wireOp",EDGE,"E69.MirrorC"),sQuery(id+"F0.wireOp",EDGE,"E70.MirrorC"),sQuery(id+"F0.wireOp",EDGE,"E71.MirrorC")])],"isStart":false});
            var sketch = newSketch(context, id + "F4", { "sketchPlane" : qUnion([Q0])});
            skLineSegment(sketch, "E172", {"start": v(0, 28) * mm, "end": v(0, 24) * mm, "construction": true});
            skLineSegment(sketch, "E173", {"start": v(-8, 28) * mm, "end": v(-8, 24) * mm, "construction": true});
            skLineSegment(sketch, "E174.MirrorCS", {"start": v(8, 28) * mm, "end": v(8, 24) * mm, "construction": true});
            skArc(sketch, "E175.0.startCap", {"start": v(-9.62, 28) * mm, "mid": v(-8, 29.62) * mm, "end": v(-6.38, 28) * mm});
            skArc(sketch, "E175.0.endCap", {"start": v(-6.38, 24) * mm, "mid": v(-8, 22.38) * mm, "end": v(-9.62, 24) * mm});
            skLineSegment(sketch, "E175.0.left", {"start": v(-6.38, 28) * mm, "end": v(-6.38, 24) * mm});
            skLineSegment(sketch, "E175.0.right", {"start": v(-9.62, 28) * mm, "end": v(-9.62, 24) * mm});
            skArc(sketch, "E175.1.startCap", {"start": v(-1.63, 28) * mm, "mid": v(0, 29.63) * mm, "end": v(1.63, 28) * mm});
            skArc(sketch, "E175.1.endCap", {"start": v(1.63, 24) * mm, "mid": v(0, 22.38) * mm, "end": v(-1.63, 24) * mm});
            skLineSegment(sketch, "E175.1.left", {"start": v(1.63, 28) * mm, "end": v(1.63, 24) * mm});
            skLineSegment(sketch, "E175.1.right", {"start": v(-1.63, 28) * mm, "end": v(-1.63, 24) * mm});
            skArc(sketch, "E175.2.startCap", {"start": v(6.38, 28) * mm, "mid": v(8, 29.62) * mm, "end": v(9.62, 28) * mm});
            skArc(sketch, "E175.2.endCap", {"start": v(9.62, 24) * mm, "mid": v(8, 22.38) * mm, "end": v(6.38, 24) * mm});
            skLineSegment(sketch, "E175.2.left", {"start": v(9.62, 28) * mm, "end": v(9.62, 24) * mm});
            skLineSegment(sketch, "E175.2.right", {"start": v(6.38, 28) * mm, "end": v(6.38, 24) * mm});
            skSolve(sketch);
        }
        {
            var Q0;
            Q0 = qSketchRegion(id + "F4", true);
            extrude(context, id + "F5", {"entities" : qUnion([Q0]), "operationType" : NewBodyOperationType.REMOVE, "oppositeDirection" : true, "depth" : 25 * mm, "offsetDistance" : 25 * mm});
        }
        {
            var Q0;
            Q0=makeQuery(id+"F1.opExtrude","CAP_FACE",FACE,{"disambiguationData":[OSD([sQuery(id+"F0.wireOp",EDGE,"E0"),sQuery(id+"F0.wireOp",EDGE,"bZv11kwC-7Zwh-qoiM-MuVD-QWfY3VRXTvEb"),sQuery(id+"F0.wireOp",EDGE,"Hg7IfRWj-3ALA-Ly6Y-QmXC-kUpIx1ZQ4bFj"),sQuery(id+"F0.wireOp",EDGE,"i2Ly1i0H-hUQD-DSDW-V0AA-PaiG6Uw8rzNW"),sQuery(id+"F0.wireOp",EDGE,"E5.bottom"),sQuery(id+"F0.wireOp",EDGE,"E5.left"),sQuery(id+"F0.wireOp",EDGE,"E5.right"),sQuery(id+"F0.wireOp",EDGE,"E7"),sQuery(id+"F0.wireOp",EDGE,"E8"),sQuery(id+"F0.wireOp",EDGE,"26a3e7e2-4a16-4030-acf8-3f1fbd5a5a34.filletArc"),sQuery(id+"F0.wireOp",EDGE,"E10.0.startCap"),sQuery(id+"F0.wireOp",EDGE,"E10.0.endCap"),sQuery(id+"F0.wireOp",EDGE,"E10.0.left"),sQuery(id+"F0.wireOp",EDGE,"E10.0.right"),sQuery(id+"F0.wireOp",EDGE,"E11.filletArc"),sQuery(id+"F0.wireOp",EDGE,"E12.filletArc"),sQuery(id+"F0.wireOp",EDGE,"E13.filletArc"),sQuery(id+"F0.wireOp",EDGE,"E14.filletArc"),sQuery(id+"F0.wireOp",EDGE,"E15.MirrorCS"),sQuery(id+"F0.wireOp",EDGE,"E16.MirrorCS"),sQuery(id+"F0.wireOp",EDGE,"E17.MirrorCS"),sQuery(id+"F0.wireOp",EDGE,"E18.MirrorCS"),sQuery(id+"F0.wireOp",EDGE,"E19.MirrorCS"),sQuery(id+"F0.wireOp",EDGE,"E20.MirrorCS"),sQuery(id+"F0.wireOp",EDGE,"b7ecff87-ac14-4935-8a3e-caa413c79c2e13.MirrorCS"),sQuery(id+"F0.wireOp",EDGE,"E21.MirrorCS"),sQuery(id+"F0.wireOp",EDGE,"E22.MirrorCS"),sQuery(id+"F0.wireOp",EDGE,"E23.MirrorCS"),sQuery(id+"F0.wireOp",EDGE,"E24.MirrorCS"),sQuery(id+"F0.wireOp",EDGE,"b7ecff87-ac14-4935-8a3e-caa413c79c2e23.MirrorCS"),sQuery(id+"F0.wireOp",EDGE,"E27.MirrorC"),sQuery(id+"F0.wireOp",EDGE,"E29.MirrorCS"),sQuery(id+"F0.wireOp",EDGE,"b7ecff87-ac14-4935-8a3e-caa413c79c2e29.MirrorCS"),sQuery(id+"F0.wireOp",EDGE,"E33.MirrorCS"),sQuery(id+"F0.wireOp",EDGE,"E34.MirrorCS"),sQuery(id+"F0.wireOp",EDGE,"b7ecff87-ac14-4935-8a3e-caa413c79c2e39.MirrorCS"),sQuery(id+"F0.wireOp",EDGE,"E38.MirrorCS"),sQuery(id+"F0.wireOp",EDGE,"E39.MirrorCS"),sQuery(id+"F0.wireOp",EDGE,"E40.MirrorCS"),sQuery(id+"F0.wireOp",EDGE,"E41.MirrorCS"),sQuery(id+"F0.wireOp",EDGE,"E42.MirrorCS"),sQuery(id+"F0.wireOp",EDGE,"E43.MirrorCS"),sQuery(id+"F0.wireOp",EDGE,"E44.MirrorCS"),sQuery(id+"F0.wireOp",EDGE,"E45.MirrorCS"),sQuery(id+"F0.wireOp",EDGE,"E46.MirrorCS"),sQuery(id+"F0.wireOp",EDGE,"E47.MirrorCS"),sQuery(id+"F0.wireOp",EDGE,"E48.MirrorCS"),sQuery(id+"F0.wireOp",EDGE,"E49.MirrorCS"),sQuery(id+"F0.wireOp",EDGE,"E50.MirrorC"),sQuery(id+"F0.wireOp",EDGE,"E51.MirrorC"),sQuery(id+"F0.wireOp",EDGE,"7b8357ce-6b81-4621-bb5f-09712327f37e37.MirrorCS"),sQuery(id+"F0.wireOp",EDGE,"E53.MirrorCS"),sQuery(id+"F0.wireOp",EDGE,"E55.MirrorCS"),sQuery(id+"F0.wireOp",EDGE,"E58.MirrorCS"),sQuery(id+"F0.wireOp",EDGE,"E59.MirrorCS"),sQuery(id+"F0.wireOp",EDGE,"E60.MirrorCS"),sQuery(id+"F0.wireOp",EDGE,"7b8357ce-6b81-4621-bb5f-09712327f37e49.MirrorCS"),sQuery(id+"F0.wireOp",EDGE,"7b8357ce-6b81-4621-bb5f-09712327f37e50.MirrorCS"),sQuery(id+"F0.wireOp",EDGE,"E62.MirrorCS"),sQuery(id+"F0.wireOp",EDGE,"7b8357ce-6b81-4621-bb5f-09712327f37e55.MirrorCS"),sQuery(id+"F0.wireOp",EDGE,"d83ce2ea-2607-4b6c-a04d-38c7ae4304c90.MirrorCS"),sQuery(id+"F0.wireOp",EDGE,"b69c18a7-e43b-42be-b145-92b5204aa2ed0.MirrorCS"),sQuery(id+"F0.wireOp",EDGE,"a0707623-7043-4475-b436-6124989390590.MirrorCS"),sQuery(id+"F0.wireOp",EDGE,"4f61c261-c1ce-4229-8802-2f54477ed9b20.MirrorCS"),sQuery(id+"F0.wireOp",EDGE,"PiAP6XZh-xq8d-wj9O-Epc7-kF4WUdjTUHBz"),sQuery(id+"F0.wireOp",EDGE,"26e37ba6-caeb-4f33-ab48-1d1fe7035cbd0.MirrorC"),sQuery(id+"F0.wireOp",EDGE,"2yan8IeJ-tOHB-Kgj5-MnLH-DyiSyil4pG3S"),sQuery(id+"F0.wireOp",EDGE,"gHJ05LQx-usyR-kV3a-hPzh-QXjW5T1wXW1p"),sQuery(id+"F0.wireOp",EDGE,"uchXSoDE-KjdM-uTwm-rJXX-9rzWfyOP3x4Z"),sQuery(id+"F0.wireOp",EDGE,"8eu2Gxre-rbZ0-mDo1-W97T-pc3IviFYihye"),sQuery(id+"F0.wireOp",EDGE,"eavqlNsN-eOFr-pDPr-DEgw-YRCTYlhg5u3t"),sQuery(id+"F0.wireOp",EDGE,"Bw8slYh4-NEub-OYFD-4ET6-0dd0G63bUOwi"),sQuery(id+"F0.wireOp",EDGE,"af94888a-cba0-45cd-aecc-a0270221dd82.trimOffspring"),sQuery(id+"F0.wireOp",EDGE,"36199e4a-d6a7-49c4-a502-27b3488fd5e6.filletArc"),sQuery(id+"F0.wireOp",EDGE,"9e30e6b1-65ef-4937-9bd8-18fed2c5f1090.MirrorCS"),sQuery(id+"F0.wireOp",EDGE,"31f30485-6f3e-4795-917b-55e225d339680.MirrorCS"),sQuery(id+"F0.wireOp",EDGE,"86aa6092-d3c3-42aa-99ce-90435510c5960.MirrorCS"),sQuery(id+"F0.wireOp",EDGE,"5a69975c-1d9b-4b23-809c-878e26df679d0.MirrorCS"),sQuery(id+"F0.wireOp",EDGE,"8025df49-7d22-4dba-957a-6396c4b11ce90.MirrorCS"),sQuery(id+"F0.wireOp",EDGE,"b23088bf-ab4c-4e44-9a43-da8ffa8499a00.MirrorCS"),sQuery(id+"F0.wireOp",EDGE,"d9780cfa-9ead-4347-a629-1b1a594d6e410.MirrorCS"),sQuery(id+"F0.wireOp",EDGE,"68fec51b-96b4-4918-b858-b07c475e679e0.MirrorCS"),sQuery(id+"F0.wireOp",EDGE,"b72a6ee6-5ab0-4ed6-be8f-ffada714514d0.MirrorCS"),sQuery(id+"F0.wireOp",EDGE,"8773bbf2-5ef2-485a-bde0-34addb67332b0.MirrorCS"),sQuery(id+"F0.wireOp",EDGE,"ce348970-fad1-4eb4-9c27-5204bf570fdb0.MirrorCS"),sQuery(id+"F0.wireOp",EDGE,"404c4f6d-7f85-4f91-8924-7a461248f6590.MirrorCS"),sQuery(id+"F0.wireOp",EDGE,"TJ6xSgkY-RBVc-ApbF-Rnxn-nYxT4uNRJTxX"),sQuery(id+"F0.wireOp",EDGE,"UOzbpYJr-Rpqu-ZeE8-tXKC-t89DSqlBGB8Q"),sQuery(id+"F0.wireOp",EDGE,"YxJJHRqV-amlc-LN3y-haml-tisoirnnfRJY"),sQuery(id+"F0.wireOp",EDGE,"033e0fe7-d3c1-42f5-ae8f-adbb043379e8.filletArc"),sQuery(id+"F0.wireOp",EDGE,"afa99035-e99d-4a73-974f-5500cdf2138a.filletArc"),sQuery(id+"F0.wireOp",EDGE,"9i3ea3iE-3Dll-Ek6R-PhGe-V1XcnAEkodY1.bottom"),sQuery(id+"F0.wireOp",EDGE,"9i3ea3iE-3Dll-Ek6R-PhGe-V1XcnAEkodY1.left"),sQuery(id+"F0.wireOp",EDGE,"9i3ea3iE-3Dll-Ek6R-PhGe-V1XcnAEkodY1.right"),sQuery(id+"F0.wireOp",EDGE,"1382622d-cae2-4c61-9f5c-b8746732d9fe0.MirrorCS"),sQuery(id+"F0.wireOp",EDGE,"0d70f9a0-c1ad-434e-a495-165a5a764f960.MirrorCS"),sQuery(id+"F0.wireOp",EDGE,"1f8d5036-162d-4fc3-b441-7a8ab5cd179e0.MirrorCS"),sQuery(id+"F0.wireOp",EDGE,"Km0E7gO1-P8tX-SnyZ-vo1L-W35BEzFtr7vK"),sQuery(id+"F0.wireOp",EDGE,"4twT0r3F-PA9R-wz1e-iyg0-9RBk79VGwi7g"),sQuery(id+"F0.wireOp",EDGE,"14bccf5c-bb99-48c5-a73f-577480a40b4e0.MirrorCS"),sQuery(id+"F0.wireOp",EDGE,"a123c59d-a695-4b06-9137-5aaff9e2b4be0.MirrorCS"),sQuery(id+"F0.wireOp",EDGE,"E68"),sQuery(id+"F0.wireOp",EDGE,"E69.MirrorC"),sQuery(id+"F0.wireOp",EDGE,"E70.MirrorC"),sQuery(id+"F0.wireOp",EDGE,"E71.MirrorC")])],"isStart":false});
            var sketch = newSketch(context, id + "F6", { "sketchPlane" : qUnion([Q0])});
            skLineSegment(sketch, "E176.bottom", {"start": v(-6, 43.5) * mm, "end": v(6, 43.5) * mm});
            skLineSegment(sketch, "E176.top", {"start": v(-6, 35.5) * mm, "end": v(6, 35.5) * mm});
            skLineSegment(sketch, "E176.left", {"start": v(-8, 41.5) * mm, "end": v(-8, 37.5) * mm});
            skLineSegment(sketch, "E176.right", {"start": v(8, 41.5) * mm, "end": v(8, 37.5) * mm});
            skPoint(sketch, "E177.visualSharp", {"position": v(-8, 43.5) * mm});
            skArc(sketch, "E177.filletArc", {"start": v(-6, 43.5) * mm, "mid": v(-7.41, 42.91) * mm, "end": v(-8, 41.5) * mm});
            skPoint(sketch, "E178.visualSharp", {"position": v(-8, 35.5) * mm});
            skArc(sketch, "E178.filletArc", {"start": v(-8, 37.5) * mm, "mid": v(-7.41, 36.09) * mm, "end": v(-6, 35.5) * mm});
            skPoint(sketch, "E179.visualSharp", {"position": v(8, 35.5) * mm});
            skArc(sketch, "E179.filletArc", {"start": v(6, 35.5) * mm, "mid": v(7.41, 36.09) * mm, "end": v(8, 37.5) * mm});
            skPoint(sketch, "E180.visualSharp", {"position": v(8, 43.5) * mm});
            skArc(sketch, "E180.filletArc", {"start": v(8, 41.5) * mm, "mid": v(7.41, 42.91) * mm, "end": v(6, 43.5) * mm});
            skLineSegment(sketch, "E181", {"start": v(-5, -28) * mm, "end": v(-5, -31) * mm, "construction": true});
            skLineSegment(sketch, "E182.MirrorCS", {"start": v(5, -28) * mm, "end": v(5, -31) * mm, "construction": true});
            skArc(sketch, "E183.0.startCap", {"start": v(-6.5, -28) * mm, "mid": v(-5, -26.5) * mm, "end": v(-3.5, -28) * mm});
            skArc(sketch, "E183.0.endCap", {"start": v(-3.5, -31) * mm, "mid": v(-5, -32.5) * mm, "end": v(-6.5, -31) * mm});
            skLineSegment(sketch, "E183.0.left", {"start": v(-3.5, -28) * mm, "end": v(-3.5, -31) * mm});
            skLineSegment(sketch, "E183.0.right", {"start": v(-6.5, -28) * mm, "end": v(-6.5, -31) * mm});
            skArc(sketch, "E183.1.startCap", {"start": v(3.5, -28) * mm, "mid": v(5, -26.5) * mm, "end": v(6.5, -28) * mm});
            skArc(sketch, "E183.1.endCap", {"start": v(6.5, -31) * mm, "mid": v(5, -32.5) * mm, "end": v(3.5, -31) * mm});
            skLineSegment(sketch, "E183.1.left", {"start": v(6.5, -28) * mm, "end": v(6.5, -31) * mm});
            skLineSegment(sketch, "E183.1.right", {"start": v(3.5, -28) * mm, "end": v(3.5, -31) * mm});
            skCircle(sketch, "E184", {"center": v(0, 0) * mm, "radius": 9 * mm});
            skSolve(sketch);
        }
        {
            var Q0;
            Q0 = qSketchRegion(id + "F6", true);
            extrude(context, id + "F7", {"entities" : qUnion([Q0]), "operationType" : NewBodyOperationType.REMOVE, "oppositeDirection" : true, "depth" : 25 * mm, "offsetDistance" : 25 * mm});
        }
        {
            var Q0;
            Q0=makeQuery(id+"F1.opExtrude","SWEPT_EDGE",EDGE,{"disambiguationData":[OSD([sQuery(id+"F0.wireOp",EDGE,"E6"),sQuery(id+"F0.wireOp",EDGE,"E86")])]});
            var Q1;
            Q1=makeQuery(id+"F1.opExtrude","SWEPT_EDGE",EDGE,{"disambiguationData":[OSD([sQuery(id+"F0.wireOp",EDGE,"E26.MirrorCS"),sQuery(id+"F0.wireOp",EDGE,"E87")])]});
            fillet(context, id + "F8", {"entities" : qUnion([Q0, Q1]), "radius" : 3 * mm, "tangentPropagation" : true, "allowEdgeOverflow" : false});
        }
        {
            var Q0;
            Q0=makeQuery(id+"F1.opExtrude","CAP_FACE",FACE,{"disambiguationData":[OSD([sQuery(id+"F0.wireOp",EDGE,"E0"),sQuery(id+"F0.wireOp",EDGE,"E5.bottom"),sQuery(id+"F0.wireOp",EDGE,"E5.left"),sQuery(id+"F0.wireOp",EDGE,"E5.right"),sQuery(id+"F0.wireOp",EDGE,"E6"),sQuery(id+"F0.wireOp",EDGE,"E7"),sQuery(id+"F0.wireOp",EDGE,"E8"),sQuery(id+"F0.wireOp",EDGE,"E10.0.startCap"),sQuery(id+"F0.wireOp",EDGE,"E10.0.endCap"),sQuery(id+"F0.wireOp",EDGE,"E10.0.left"),sQuery(id+"F0.wireOp",EDGE,"E10.0.right"),sQuery(id+"F0.wireOp",EDGE,"E11.filletArc"),sQuery(id+"F0.wireOp",EDGE,"E12.filletArc"),sQuery(id+"F0.wireOp",EDGE,"E13.filletArc"),sQuery(id+"F0.wireOp",EDGE,"E14.filletArc"),sQuery(id+"F0.wireOp",EDGE,"E15.MirrorCS"),sQuery(id+"F0.wireOp",EDGE,"E16.MirrorCS"),sQuery(id+"F0.wireOp",EDGE,"E17.MirrorCS"),sQuery(id+"F0.wireOp",EDGE,"E18.MirrorCS"),sQuery(id+"F0.wireOp",EDGE,"E19.MirrorCS"),sQuery(id+"F0.wireOp",EDGE,"E20.MirrorCS"),sQuery(id+"F0.wireOp",EDGE,"E21.MirrorCS"),sQuery(id+"F0.wireOp",EDGE,"E22.MirrorCS"),sQuery(id+"F0.wireOp",EDGE,"E23.MirrorCS"),sQuery(id+"F0.wireOp",EDGE,"E24.MirrorCS"),sQuery(id+"F0.wireOp",EDGE,"E26.MirrorCS"),sQuery(id+"F0.wireOp",EDGE,"E27.MirrorC"),sQuery(id+"F0.wireOp",EDGE,"E29.MirrorCS"),sQuery(id+"F0.wireOp",EDGE,"E33.MirrorCS"),sQuery(id+"F0.wireOp",EDGE,"E34.MirrorCS"),sQuery(id+"F0.wireOp",EDGE,"E38.MirrorCS"),sQuery(id+"F0.wireOp",EDGE,"E39.MirrorCS"),sQuery(id+"F0.wireOp",EDGE,"E40.MirrorCS"),sQuery(id+"F0.wireOp",EDGE,"E41.MirrorCS"),sQuery(id+"F0.wireOp",EDGE,"E42.MirrorCS"),sQuery(id+"F0.wireOp",EDGE,"E43.MirrorCS"),sQuery(id+"F0.wireOp",EDGE,"E44.MirrorCS"),sQuery(id+"F0.wireOp",EDGE,"E45.MirrorCS"),sQuery(id+"F0.wireOp",EDGE,"E46.MirrorCS"),sQuery(id+"F0.wireOp",EDGE,"E47.MirrorCS"),sQuery(id+"F0.wireOp",EDGE,"E48.MirrorCS"),sQuery(id+"F0.wireOp",EDGE,"E49.MirrorCS"),sQuery(id+"F0.wireOp",EDGE,"E50.MirrorC"),sQuery(id+"F0.wireOp",EDGE,"E51.MirrorC"),sQuery(id+"F0.wireOp",EDGE,"E53.MirrorCS"),sQuery(id+"F0.wireOp",EDGE,"E55.MirrorCS"),sQuery(id+"F0.wireOp",EDGE,"E58.MirrorCS"),sQuery(id+"F0.wireOp",EDGE,"E59.MirrorCS"),sQuery(id+"F0.wireOp",EDGE,"E60.MirrorCS"),sQuery(id+"F0.wireOp",EDGE,"E62.MirrorCS"),sQuery(id+"F0.wireOp",EDGE,"PiAP6XZh-xq8d-wj9O-Epc7-kF4WUdjTUHBz"),sQuery(id+"F0.wireOp",EDGE,"E68"),sQuery(id+"F0.wireOp",EDGE,"E69.MirrorC"),sQuery(id+"F0.wireOp",EDGE,"E70.MirrorC"),sQuery(id+"F0.wireOp",EDGE,"E71.MirrorC"),sQuery(id+"F0.wireOp",EDGE,"saBew1CV-SxRc-ZB9K-e4XU-TCJo4jc1kgwB"),sQuery(id+"F0.wireOp",EDGE,"As7GNjuw-uwTQ-EC8a-4VWo-RmuX3ZlHdixJ"),sQuery(id+"F0.wireOp",EDGE,"17ac02e8-9e55-49a8-8953-3050a0e1ff9d.trimOffspring"),sQuery(id+"F0.wireOp",EDGE,"fgNwwMFg-OnY8-yskJ-sLJ1-vSz1G99tKk8o"),sQuery(id+"F0.wireOp",EDGE,"jiS4iSMn-SGWw-wNEF-CNbn-W2Xm5X2EO89s"),sQuery(id+"F0.wireOp",EDGE,"a3419795-80d2-4dbb-87c2-bbe54f5cbc13.trimOffspring"),sQuery(id+"F0.wireOp",EDGE,"2f9ed6c8-7ab2-4140-a752-6b7fb87077802.MirrorCS"),sQuery(id+"F0.wireOp",EDGE,"2f9ed6c8-7ab2-4140-a752-6b7fb87077807.MirrorCS"),sQuery(id+"F0.wireOp",EDGE,"2f9ed6c8-7ab2-4140-a752-6b7fb87077808.MirrorCS"),sQuery(id+"F0.wireOp",EDGE,"2f9ed6c8-7ab2-4140-a752-6b7fb870778010.MirrorCS"),sQuery(id+"F0.wireOp",EDGE,"2f9ed6c8-7ab2-4140-a752-6b7fb870778011.MirrorCS"),sQuery(id+"F0.wireOp",EDGE,"2f9ed6c8-7ab2-4140-a752-6b7fb870778012.MirrorCS"),sQuery(id+"F0.wireOp",EDGE,"2f9ed6c8-7ab2-4140-a752-6b7fb870778014.MirrorCS"),sQuery(id+"F0.wireOp",EDGE,"E72"),sQuery(id+"F0.wireOp",EDGE,"E73.MirrorCS"),sQuery(id+"F0.wireOp",EDGE,"E74.MirrorCS"),sQuery(id+"F0.wireOp",EDGE,"E75.MirrorCS"),sQuery(id+"F0.wireOp",EDGE,"E76.trimOffspring"),sQuery(id+"F0.wireOp",EDGE,"E77.MirrorCS"),sQuery(id+"F0.wireOp",EDGE,"E78.MirrorCS"),sQuery(id+"F0.wireOp",EDGE,"E79.MirrorCS"),sQuery(id+"F0.wireOp",EDGE,"E80"),sQuery(id+"F0.wireOp",EDGE,"E81.filletArc"),sQuery(id+"F0.wireOp",EDGE,"E82.filletArc"),sQuery(id+"F0.wireOp",EDGE,"E83.filletArc"),sQuery(id+"F0.wireOp",EDGE,"E84.filletArc"),sQuery(id+"F0.wireOp",EDGE,"E85"),sQuery(id+"F0.wireOp",EDGE,"E86"),sQuery(id+"F0.wireOp",EDGE,"E87"),sQuery(id+"F0.wireOp",EDGE,"E88.filletArc"),sQuery(id+"F0.wireOp",EDGE,"E89.filletArc"),sQuery(id+"F0.wireOp",EDGE,"E90.MirrorC"),sQuery(id+"F0.wireOp",EDGE,"E91.filletArc"),sQuery(id+"F0.wireOp",EDGE,"E92.filletArc")])],"isStart":false});
            var sketch = newSketch(context, id + "F9", { "sketchPlane" : qUnion([Q0])});
            skLineSegment(sketch, "E185", {"start": v(-94.34, -82) * mm, "end": v(0, -12) * mm, "construction": true});
            skLineSegment(sketch, "E186", {"start": v(-94.34, -82) * mm, "end": v(-107.19, -91.54) * mm, "construction": true});
            skLineSegment(sketch, "E187", {"start": v(-94.34, 82) * mm, "end": v(0, 12) * mm, "construction": true});
            skArc(sketch, "E188", {"start": v(-29.05, 34.78) * mm, "mid": v(-23.82, 32.1) * mm, "end": v(-18.56, 29.48) * mm});
            skArc(sketch, "E189.MirrorCS", {"start": v(-30.22, 33.2) * mm, "mid": v(-24.93, 27.71) * mm, "end": v(-19.74, 22.13) * mm});
            skLineSegment(sketch, "E190", {"start": v(-18, 28.58) * mm, "end": v(-18, 22.8) * mm});
            skPoint(sketch, "E191.visualSharp", {"position": v(-35, 37.97) * mm});
            skArc(sketch, "E191.filletArc", {"start": v(-29.05, 34.78) * mm, "mid": v(-30.31, 34.5) * mm, "end": v(-30.22, 33.2) * mm});
            skPoint(sketch, "E192.visualSharp", {"position": v(-18, 29.2) * mm});
            skArc(sketch, "E192.filletArc", {"start": v(-18, 28.58) * mm, "mid": v(-18.15, 29.1) * mm, "end": v(-18.56, 29.48) * mm});
            skPoint(sketch, "E193.visualSharp", {"position": v(-18, 20.2) * mm});
            skArc(sketch, "E193.filletArc", {"start": v(-19.74, 22.13) * mm, "mid": v(-18.64, 21.87) * mm, "end": v(-18, 22.8) * mm});
            skArc(sketch, "E194.MirrorCS", {"start": v(18, 28.58) * mm, "mid": v(18.15, 29.1) * mm, "end": v(18.56, 29.48) * mm});
            skArc(sketch, "E195.MirrorCS", {"start": v(19.74, 22.13) * mm, "mid": v(18.64, 21.87) * mm, "end": v(18, 22.8) * mm});
            skArc(sketch, "E196.MirrorCS", {"start": v(29.05, 34.78) * mm, "mid": v(30.31, 34.5) * mm, "end": v(30.22, 33.2) * mm});
            skPoint(sketch, "E197.MirrorP", {"position": v(18, 20.2) * mm});
            skArc(sketch, "E198.MirrorCS", {"start": v(29.05, 34.78) * mm, "mid": v(23.82, 32.1) * mm, "end": v(18.56, 29.48) * mm});
            skPoint(sketch, "E199.MirrorP", {"position": v(18, 29.2) * mm});
            skArc(sketch, "E200.MirrorCS", {"start": v(30.22, 33.2) * mm, "mid": v(24.93, 27.71) * mm, "end": v(19.74, 22.13) * mm});
            skLineSegment(sketch, "E201.MirrorCS", {"start": v(18, 28.58) * mm, "end": v(18, 22.8) * mm});
            skArc(sketch, "E202.MirrorCS", {"start": v(18, -28.58) * mm, "mid": v(18.15, -29.1) * mm, "end": v(18.56, -29.48) * mm});
            skArc(sketch, "E203.MirrorCS", {"start": v(29.05, -34.78) * mm, "mid": v(30.31, -34.5) * mm, "end": v(30.22, -33.2) * mm});
            skArc(sketch, "E204.MirrorCS", {"start": v(19.74, -22.13) * mm, "mid": v(18.64, -21.87) * mm, "end": v(18, -22.8) * mm});
            skPoint(sketch, "E205.MirrorP", {"position": v(18, -29.2) * mm});
            skLineSegment(sketch, "E206.MirrorCS", {"start": v(18, -28.58) * mm, "end": v(18, -22.8) * mm});
            skPoint(sketch, "E207.MirrorP", {"position": v(18, -20.2) * mm});
            skArc(sketch, "E208.MirrorCS", {"start": v(29.05, -34.78) * mm, "mid": v(23.82, -32.1) * mm, "end": v(18.56, -29.48) * mm});
            skArc(sketch, "E209.MirrorCS", {"start": v(30.22, -33.2) * mm, "mid": v(24.93, -27.71) * mm, "end": v(19.74, -22.13) * mm});
            skArc(sketch, "E210.MirrorCS", {"start": v(-18, -28.58) * mm, "mid": v(-18.15, -29.1) * mm, "end": v(-18.56, -29.48) * mm});
            skArc(sketch, "E211.MirrorCS", {"start": v(-19.74, -22.13) * mm, "mid": v(-18.64, -21.87) * mm, "end": v(-18, -22.8) * mm});
            skArc(sketch, "E212.MirrorCS", {"start": v(-29.05, -34.78) * mm, "mid": v(-30.31, -34.5) * mm, "end": v(-30.22, -33.2) * mm});
            skArc(sketch, "E213.MirrorCS", {"start": v(-30.22, -33.2) * mm, "mid": v(-24.93, -27.71) * mm, "end": v(-19.74, -22.13) * mm});
            skPoint(sketch, "E214.MirrorP", {"position": v(-18, -29.2) * mm});
            skArc(sketch, "E215.MirrorCS", {"start": v(-29.05, -34.78) * mm, "mid": v(-23.82, -32.1) * mm, "end": v(-18.56, -29.48) * mm});
            skLineSegment(sketch, "E216.MirrorCS", {"start": v(-18, -28.58) * mm, "end": v(-18, -22.8) * mm});
            skPoint(sketch, "E217.MirrorP", {"position": v(-18, -20.2) * mm});
            skSolve(sketch);
        }
        {
            var Q0;
            Q0 = qSketchRegion(id + "F9", true);
            extrude(context, id + "F10", {"entities" : qUnion([Q0]), "operationType" : NewBodyOperationType.REMOVE, "oppositeDirection" : true, "depth" : 25 * mm, "offsetDistance" : 25 * mm});
        }
        {
            var Q0;
            Q0=qCreatedBy(makeId("Top.planeOp"),FACE);
            var sketch = newSketch(context, id + "F11", { "sketchPlane" : qUnion([Q0])});
            skLineSegment(sketch, "E218.bottom", {"start": v(-92.7, 60.74) * mm, "end": v(-112.85, 75.7) * mm});
            skLineSegment(sketch, "E218.top", {"start": v(-73.5, 86.6) * mm, "end": v(-93.66, 101.55) * mm});
            skLineSegment(sketch, "E218.left", {"start": v(-91, 59.48) * mm, "end": v(-71.82, 85.34) * mm, "construction": true});
            skLineSegment(sketch, "E218.right", {"start": v(-113.88, 82.69) * mm, "end": v(-100.65, 100.52) * mm});
            skPoint(sketch, "E218.middle", {"position": v(-94.34, 82) * mm});
            skPoint(sketch, "E219.visualSharp", {"position": v(-97.67, 104.53) * mm});
            skArc(sketch, "E219.filletArc", {"start": v(-93.66, 101.55) * mm, "mid": v(-97.37, 102.48) * mm, "end": v(-100.65, 100.52) * mm});
            skPoint(sketch, "E220.visualSharp", {"position": v(-116.86, 78.67) * mm});
            skArc(sketch, "E220.filletArc", {"start": v(-113.88, 82.69) * mm, "mid": v(-114.81, 78.98) * mm, "end": v(-112.85, 75.7) * mm});
            skLineSegment(sketch, "E221", {"start": v(-71.52, 83.22) * mm, "end": v(-88.89, 59.82) * mm});
            skArc(sketch, "E222", {"start": v(-92.7, 60.74) * mm, "mid": v(-90.88, 59.89) * mm, "end": v(-88.89, 59.82) * mm});
            skLineSegment(sketch, "E223", {"start": v(-107.27, 91.6) * mm, "end": v(-81.4, 72.41) * mm, "construction": true});
            skArc(sketch, "E224.MirrorCS", {"start": v(-73.5, 86.6) * mm, "mid": v(-72.17, 85.1) * mm, "end": v(-71.52, 83.22) * mm});
            skArc(sketch, "E225.0", {"start": v(-93.88, 59.13) * mm, "mid": v(-92.23, 58.22) * mm, "end": v(-90.4, 57.78) * mm});
            skLineSegment(sketch, "E225.1", {"start": v(-93.88, 59.13) * mm, "end": v(-114.04, 74.09) * mm});
            skArc(sketch, "E225.2", {"start": v(-115.49, 83.88) * mm, "mid": v(-116.8, 78.68) * mm, "end": v(-114.04, 74.09) * mm});
            skArc(sketch, "E225.3", {"start": v(-72.3, 88.2) * mm, "mid": v(-70.96, 86.88) * mm, "end": v(-70.01, 85.25) * mm});
            skLineSegment(sketch, "E225.4", {"start": v(-72.3, 88.2) * mm, "end": v(-92.47, 103.16) * mm});
            skArc(sketch, "E225.5", {"start": v(-92.47, 103.16) * mm, "mid": v(-97.66, 104.46) * mm, "end": v(-102.26, 101.7) * mm});
            skLineSegment(sketch, "E225.6", {"start": v(-115.49, 83.88) * mm, "end": v(-102.26, 101.7) * mm});
            skLineSegment(sketch, "E226", {"start": v(-88.89, 59.82) * mm, "end": v(-90.4, 57.78) * mm});
            skLineSegment(sketch, "E227", {"start": v(-71.52, 83.22) * mm, "end": v(-70.01, 85.25) * mm});
            skSolve(sketch);
        }
        {
            var Q0;
            Q0=makeQuery(id+"F11.imprint","IMPRINT",FACE,{"disambiguationData":[TD([[makeQuery(id+"F11.imprint","IMPRINT",EDGE,{"derivedFrom":sQuery(id+"F11.wireOp",EDGE,"E218.bottom")}),1.0]])]});
            var Q1;
            Q1=makeQuery(id+"F11.imprint","IMPRINT",FACE,{"disambiguationData":[TD([[makeQuery(id+"F11.imprint","IMPRINT",EDGE,{"derivedFrom":sQuery(id+"F11.wireOp",EDGE,"E218.bottom")}),-1.0]])]});
            extrude(context, id + "F12", {"entities" : qUnion([Q0, Q1]), "depth" : 8.1 * mm, "offsetDistance" : 25 * mm});
        }
        {
            var Q0;
            Q0=makeQuery(id+"F11.imprint","IMPRINT",FACE,{"disambiguationData":[TD([[makeQuery(id+"F11.imprint","IMPRINT",EDGE,{"derivedFrom":sQuery(id+"F11.wireOp",EDGE,"E218.bottom")}),-1.0]])]});
            extrude(context, id + "F13", {"entities" : qUnion([Q0]), "operationType" : NewBodyOperationType.REMOVE, "depth" : 6.1 * mm, "offsetDistance" : 25 * mm, "hasSecondDirection" : true, "secondDirectionOppositeDirection" : false, "secondDirectionDepth" : 2 * mm});
        }
        {
            var Q0;
            Q0=makeQuery(id+"F11.imprint","IMPRINT",FACE,{"disambiguationData":[TD([[makeQuery(id+"F11.imprint","IMPRINT",EDGE,{"derivedFrom":sQuery(id+"F11.wireOp",EDGE,"E218.bottom")}),-1.0]])]});
            var sketch = newSketch(context, id + "F14", { "sketchPlane" : qUnion([Q0])});
            skArc(sketch, "E228", {"start": v(-80.6, 86.62) * mm, "mid": v(-105.98, 90.65) * mm, "end": v(-94.77, 67.51) * mm});
            skLineSegment(sketch, "E229", {"start": v(-108.87, 92.8) * mm, "end": v(-80.2, 71.52) * mm, "construction": true});
            skLineSegment(sketch, "E230", {"start": v(-91.94, 66.53) * mm, "end": v(-86.76, 62.69) * mm});
            skLineSegment(sketch, "E231", {"start": v(-86.76, 62.69) * mm, "end": v(-73.65, 80.35) * mm});
            skLineSegment(sketch, "E232", {"start": v(-73.65, 80.35) * mm, "end": v(-78.83, 84.2) * mm});
            skPoint(sketch, "E233.visualSharp", {"position": v(-93.3, 67.54) * mm});
            skArc(sketch, "E233.filletArc", {"start": v(-91.94, 66.53) * mm, "mid": v(-93.28, 67.24) * mm, "end": v(-94.77, 67.51) * mm});
            skPoint(sketch, "E234.visualSharp", {"position": v(-80.2, 85.21) * mm});
            skArc(sketch, "E234.filletArc", {"start": v(-80.6, 86.62) * mm, "mid": v(-79.9, 85.28) * mm, "end": v(-78.83, 84.2) * mm});
            skSolve(sketch);
        }
        {
            var Q0;
            Q0=makeQuery(id+"F14.imprint","IMPRINT",FACE,{"disambiguationData":[TD([[makeQuery(id+"F14.imprint","IMPRINT",EDGE,{"derivedFrom":sQuery(id+"F14.wireOp",EDGE,"E228")}),1.0]])]});
            extrude(context, id + "F15", {"entities" : qUnion([Q0]), "operationType" : NewBodyOperationType.REMOVE, "depth" : 10 * mm, "offsetDistance" : 25 * mm, "hasSecondDirection" : true, "secondDirectionOppositeDirection" : false, "secondDirectionDepth" : 5 * mm});
        }
        {
            var Q0;
            Q0=makeQuery(id+"F12.opExtrude","CAP_FACE",FACE,{"disambiguationData":[OSD([sQuery(id+"F11.wireOp",EDGE,"E221"),sQuery(id+"F11.wireOp",EDGE,"E225.0"),sQuery(id+"F11.wireOp",EDGE,"E225.1"),sQuery(id+"F11.wireOp",EDGE,"E225.2"),sQuery(id+"F11.wireOp",EDGE,"E225.3"),sQuery(id+"F11.wireOp",EDGE,"E225.4"),sQuery(id+"F11.wireOp",EDGE,"E225.5"),sQuery(id+"F11.wireOp",EDGE,"E225.6"),sQuery(id+"F11.wireOp",EDGE,"E226"),sQuery(id+"F11.wireOp",EDGE,"E227")])],"isStart":true});
            var sketch = newSketch(context, id + "F16", { "sketchPlane" : qUnion([Q0])});
            skLineSegment(sketch, "E235", {"start": v(-108.87, -92.8) * mm, "end": v(-80.2, -71.52) * mm, "construction": true});
            skCircle(sketch, "E236", {"center": v(-94.54, -82.16) * mm, "radius": 13 * mm});
            skSolve(sketch);
        }
        {
            var Q0;
            Q0=makeQuery(id+"F16.imprint","IMPRINT",FACE,{"disambiguationData":[TD([[makeQuery(id+"F16.imprint","IMPRINT",EDGE,{"derivedFrom":sQuery(id+"F16.wireOp",EDGE,"E236")}),1.0]])]});
            extrude(context, id + "F17", {"entities" : qUnion([Q0]), "operationType" : NewBodyOperationType.REMOVE, "oppositeDirection" : true, "depth" : 25 * mm, "offsetDistance" : 25 * mm});
        }
    });
